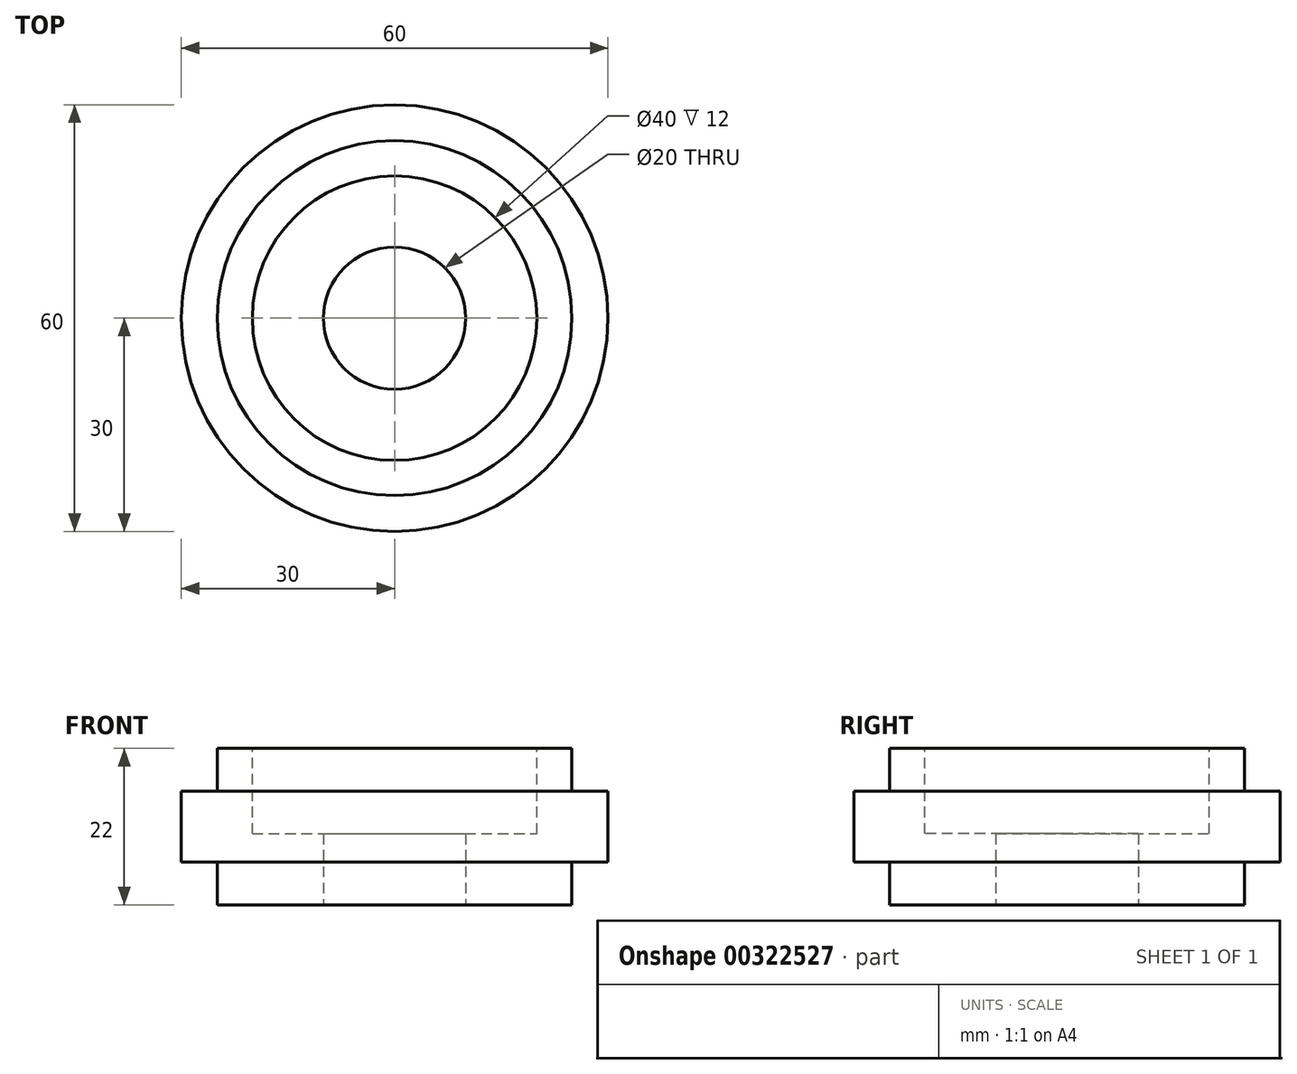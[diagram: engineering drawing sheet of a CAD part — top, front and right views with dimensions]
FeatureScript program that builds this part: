
annotation { "Feature Type Name" : "Feature", "Feature Type Description" : "" }
export const myFeature = defineFeature(function(context is Context, id is Id, definition is map)
    precondition{}
    {
        {
            var Q0;
            Q0=qCreatedBy(makeId("Top.planeOp"),FACE);
            var sketch = newSketch(context, id + "F0", { "sketchPlane" : qUnion([Q0])});
            skCircle(sketch, "E0", {"center": v(0, 0) * mm, "radius": 24.95 * mm});
            skSolve(sketch);
        }
        {
            var Q0;
            Q0 = qSketchRegion(id + "F0", true);
            extrude(context, id + "F1", {"entities" : qUnion([Q0]), "depth" : 6 * mm});
        }
        {
            var Q0;
            Q0=makeQuery(id+"F1.opExtrude","CAP_FACE",FACE,{"disambiguationData":[OSD([sQuery(id+"F0.wireOp",EDGE,"E0")])],"isStart":false});
            var sketch = newSketch(context, id + "F2", { "sketchPlane" : qUnion([Q0])});
            skCircle(sketch, "E1", {"center": v(0, 0) * mm, "radius": 30 * mm});
            skSolve(sketch);
        }
        {
            var Q0;
            Q0 = qSketchRegion(id + "F2", true);
            extrude(context, id + "F3", {"entities" : qUnion([Q0]), "operationType" : NewBodyOperationType.ADD, "depth" : 10 * mm});
        }
        {
            var Q0;
            Q0=makeQuery(id+"F3.opExtrude","CAP_FACE",FACE,{"disambiguationData":[OSD([sQuery(id+"F2.wireOp",EDGE,"E1")])],"isStart":false});
            var sketch = newSketch(context, id + "F4", { "sketchPlane" : qUnion([Q0])});
            skCircle(sketch, "E2", {"center": v(0, 0) * mm, "radius": 24.95 * mm});
            skSolve(sketch);
        }
        {
            var Q0;
            Q0 = qSketchRegion(id + "F4", true);
            extrude(context, id + "F5", {"entities" : qUnion([Q0]), "operationType" : NewBodyOperationType.ADD, "depth" : 6 * mm});
        }
        {
            var Q0;
            Q0=makeQuery(id+"F5.opExtrude","CAP_FACE",FACE,{"disambiguationData":[OSD([sQuery(id+"F4.wireOp",EDGE,"E2")])],"isStart":false});
            var sketch = newSketch(context, id + "F6", { "sketchPlane" : qUnion([Q0])});
            skCircle(sketch, "E3", {"center": v(0, 0) * mm, "radius": 20 * mm});
            skSolve(sketch);
        }
        {
            var Q0;
            Q0 = qSketchRegion(id + "F6", true);
            extrude(context, id + "F7", {"entities" : qUnion([Q0]), "operationType" : NewBodyOperationType.REMOVE, "endBound" : BoundingType.THROUGH_ALL, "oppositeDirection" : true, "depth" : 25 * mm});
        }
        {
            var Q0;
            Q0=makeQuery(id+"F1.opExtrude","CAP_FACE",FACE,{"disambiguationData":[OSD([sQuery(id+"F0.wireOp",EDGE,"E0")])],"isStart":true});
            var sketch = newSketch(context, id + "F8", { "sketchPlane" : qUnion([Q0])});
            skCircle(sketch, "E4", {"center": v(0, 0) * mm, "radius": 24.95 * mm});
            skCircle(sketch, "E5", {"center": v(0, 0) * mm, "radius": 10 * mm});
            skSolve(sketch);
        }
        {
            var Q0;
            Q0 = qSketchRegion(id + "F8", true);
            extrude(context, id + "F9", {"entities" : qUnion([Q0]), "operationType" : NewBodyOperationType.ADD, "oppositeDirection" : true, "depth" : 10 * mm});
        }
    });
